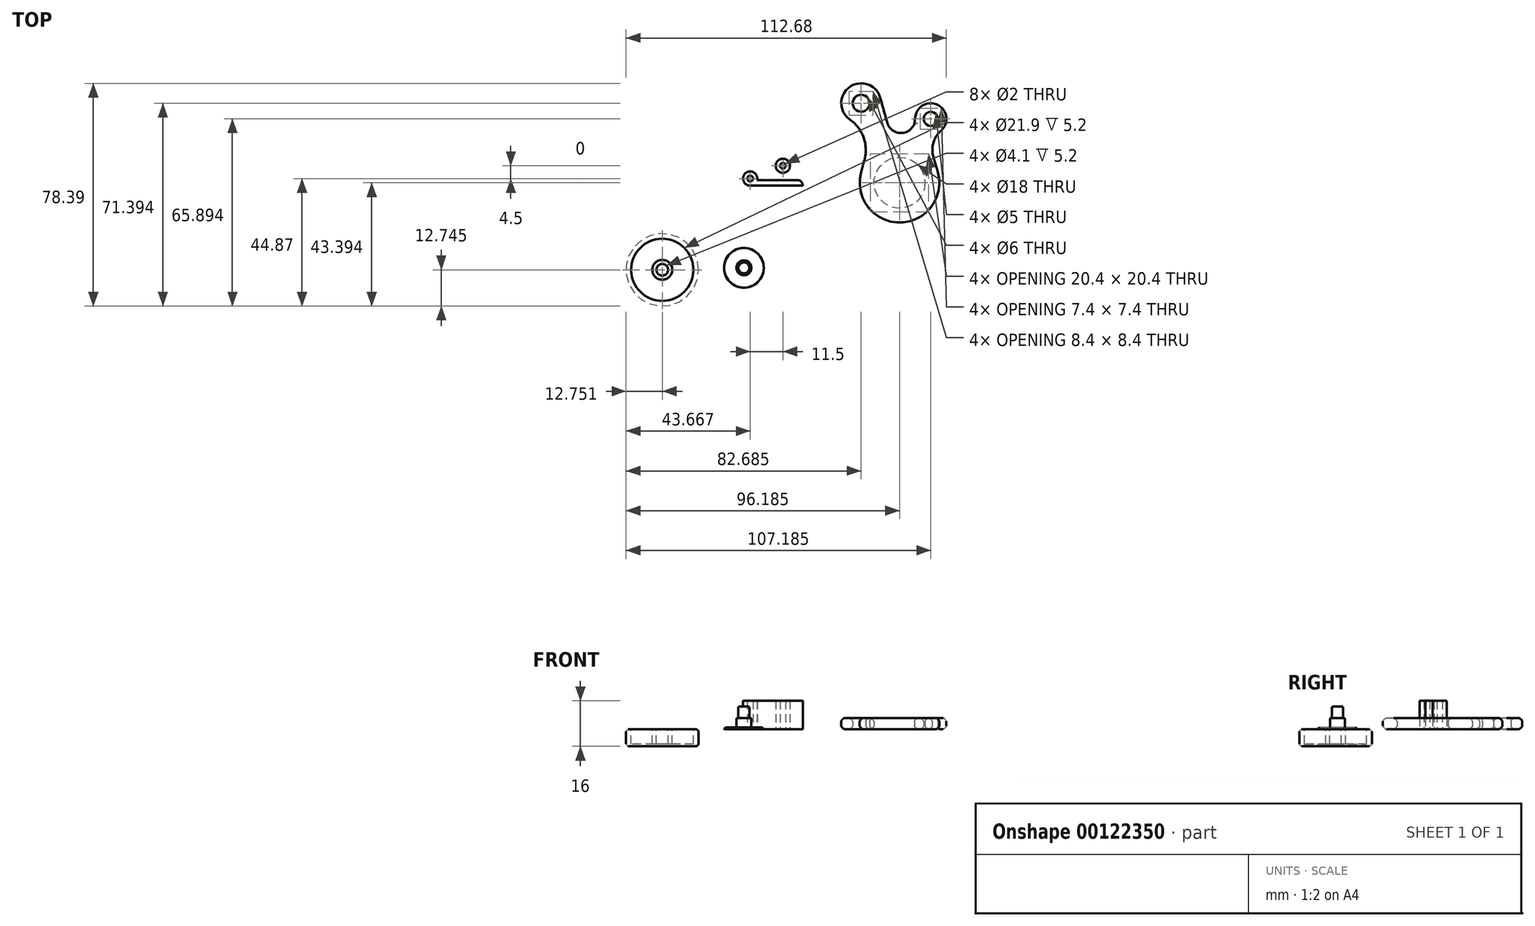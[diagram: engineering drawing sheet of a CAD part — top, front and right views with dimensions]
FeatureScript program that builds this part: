
annotation { "Feature Type Name" : "Feature", "Feature Type Description" : "" }
export const myFeature = defineFeature(function(context is Context, id is Id, definition is map)
    precondition{}
    {
        {
            var Q0;
            Q0=qCreatedBy(makeId("Top.planeOp"),FACE);
            var sketch = newSketch(context, id + "F0", { "sketchPlane" : qUnion([Q0])});
            skCircle(sketch, "E0", {"center": v(-12.84, 2.5) * mm, "radius": 2.5 * mm});
            skCircle(sketch, "E1", {"center": v(-12.84, 2.5) * mm, "radius": 1 * mm});
            skLineSegment(sketch, "E2", {"start": v(-12.84, 0) * mm, "end": v(5.66, 0) * mm});
            skLineSegment(sketch, "E3", {"start": v(-15.34, 2.5) * mm, "end": v(-15.34, 0.8) * mm});
            skArc(sketch, "E4", {"start": v(5.66, 0) * mm, "mid": v(5.07, 1.41) * mm, "end": v(3.66, 2) * mm});
            skLineSegment(sketch, "E5", {"start": v(3.66, 2) * mm, "end": v(-10.4, 2) * mm});
            skCircle(sketch, "E6", {"center": v(-1.34, 7) * mm, "radius": 1 * mm});
            skCircle(sketch, "E7", {"center": v(-1.34, 7) * mm, "radius": 2.5 * mm});
            skArc(sketch, "E8", {"start": v(-1.47, 9.5) * mm, "mid": v(-9.08, 11.1) * mm, "end": v(-13.7, 4.84) * mm});
            skLineSegment(sketch, "E9", {"start": v(-6.52, 11.57) * mm, "end": v(-11.51, 11.57) * mm});
            skArc(sketch, "E10", {"start": v(-11.32, 4.49) * mm, "mid": v(-8.57, 8.7) * mm, "end": v(-3.56, 8.15) * mm});
            skCircle(sketch, "E11", {"center": v(26.17, 29.02) * mm, "radius": 3 * mm});
            skCircle(sketch, "E12", {"center": v(26.17, 29.02) * mm, "radius": 7 * mm});
            skCircle(sketch, "E13", {"center": v(50.67, 23.52) * mm, "radius": 2.5 * mm});
            skCircle(sketch, "E14", {"center": v(50.67, 23.52) * mm, "radius": 5.5 * mm});
            skCircle(sketch, "E15", {"center": v(39.67, 1.02) * mm, "radius": 14 * mm});
            skCircle(sketch, "E16", {"center": v(39.67, 1.02) * mm, "radius": 9 * mm});
            skLineSegment(sketch, "E17", {"start": v(19.17, 29.02) * mm, "end": v(19.17, 34.36) * mm});
            skLineSegment(sketch, "E18", {"start": v(56.17, 23.52) * mm, "end": v(56.17, 35.81) * mm});
            skLineSegment(sketch, "E19", {"start": v(26.17, 36.02) * mm, "end": v(44.62, 36.02) * mm});
            skLineSegment(sketch, "E20", {"start": v(39.67, -12.98) * mm, "end": v(58, -12.98) * mm});
            skLineSegment(sketch, "E21", {"start": v(44.95, 22.03) * mm, "end": v(45.22, 24.2) * mm});
            skLineSegment(sketch, "E22", {"start": v(32.92, 30.91) * mm, "end": v(35.36, 22.18) * mm});
            skArc(sketch, "E23", {"start": v(35.36, 22.18) * mm, "mid": v(40.1, 18.52) * mm, "end": v(44.95, 22.03) * mm});
            skLineSegment(sketch, "E24", {"start": v(26.15, 4.64) * mm, "end": v(27.37, 9.2) * mm});
            skArc(sketch, "E25", {"start": v(27.37, 9.2) * mm, "mid": v(27.01, 17.05) * mm, "end": v(22.2, 23.26) * mm});
            skLineSegment(sketch, "E26", {"start": v(53.08, 5.07) * mm, "end": v(51.6, 9.93) * mm});
            skArc(sketch, "E27", {"start": v(51.6, 9.93) * mm, "mid": v(51.57, 15.06) * mm, "end": v(54.3, 19.4) * mm});
            skCircle(sketch, "E28", {"center": v(-43.76, -29.62) * mm, "radius": 12.75 * mm});
            skCircle(sketch, "E29.0", {"center": v(-43.76, -29.62) * mm, "radius": 10.95 * mm});
            skCircle(sketch, "E30", {"center": v(-43.76, -29.62) * mm, "radius": 3.5 * mm});
            skCircle(sketch, "E31", {"center": v(-43.76, -29.62) * mm, "radius": 2.05 * mm});
            skCircle(sketch, "E32", {"center": v(-15.05, -28.93) * mm, "radius": 7 * mm});
            skCircle(sketch, "E33", {"center": v(-15.05, -28.93) * mm, "radius": 2.6 * mm});
            skCircle(sketch, "E34", {"center": v(-15.05, -28.93) * mm, "radius": 1.95 * mm});
            skSolve(sketch);
        }
        {
            var Q0;
            Q0=makeQuery(id+"F0.imprint","IMPRINT",FACE,{"disambiguationData":[TD([[makeQuery(id+"F0.imprint","IMPRINT",EDGE,{"derivedFrom":sQuery(id+"F0.wireOp",EDGE,"E6")}),-1.0]])]});
            var Q1;
            {var subQ6=sQuery(id+"F0.wireOp",EDGE,"E10");Q1=makeQuery(id+"F0.imprint","IMPRINT",FACE,{"disambiguationData":[TD([[makeQuery(id+"F0.imprint","IMPRINT",EDGE,{"derivedFrom":subQ6}),1.0]])]});}
            var Q2;
            Q2=makeQuery(id+"F0.imprint","IMPRINT",FACE,{"disambiguationData":[TD([[makeQuery(id+"F0.imprint","IMPRINT",EDGE,{"derivedFrom":sQuery(id+"F0.wireOp",EDGE,"E1")}),-1.0]])]});
            var Q3;
            {var subQ0=sQuery(id+"F0.wireOp",EDGE,"E2");Q3=makeQuery(id+"F0.imprint","IMPRINT",FACE,{"disambiguationData":[TD([[makeQuery(id+"F0.imprint","IMPRINT",EDGE,{"derivedFrom":subQ0}),1.0]])]});}
            extrude(context, id + "F1", {"entities" : qUnion([Q0, Q1, Q2, Q3]), "depth" : 10 * mm});
        }
        {
            var Q0;
            {var subQ0=sQuery(id+"F0.wireOp",EDGE,"E21");Q0=makeQuery(id+"F0.imprint","IMPRINT",FACE,{"disambiguationData":[TD([[makeQuery(id+"F0.imprint","IMPRINT",EDGE,{"derivedFrom":subQ0}),-1.0]])]});}
            var Q1;
            Q1=makeQuery(id+"F0.imprint","IMPRINT",FACE,{"disambiguationData":[TD([[makeQuery(id+"F0.imprint","IMPRINT",EDGE,{"derivedFrom":sQuery(id+"F0.wireOp",EDGE,"E11")}),-1.0]])]});
            var Q2;
            Q2=makeQuery(id+"F0.imprint","IMPRINT",FACE,{"disambiguationData":[TD([[makeQuery(id+"F0.imprint","IMPRINT",EDGE,{"derivedFrom":sQuery(id+"F0.wireOp",EDGE,"E13")}),-1.0]])]});
            var Q3;
            Q3=makeQuery(id+"F0.imprint","IMPRINT",FACE,{"disambiguationData":[TD([[makeQuery(id+"F0.imprint","IMPRINT",EDGE,{"derivedFrom":sQuery(id+"F0.wireOp",EDGE,"E16")}),-1.0]])]});
            extrude(context, id + "F2", {"entities" : qUnion([Q0, Q1, Q2, Q3]), "depth" : 4 * mm});
        }
        {
            var Q0;
            Q0=makeQuery(id+"F2.opExtrude","SWEPT_FACE",FACE,{"disambiguationData":[OSD([sQuery(id+"F0.wireOp",EDGE,"E16")])]});
            var Q1;
            Q1=makeQuery(id+"F2.opExtrude","SWEPT_FACE",FACE,{"disambiguationData":[OSD([sQuery(id+"F0.wireOp",EDGE,"E15")])]});
            var Q2;
            Q2=makeQuery(id+"F2.opExtrude","SWEPT_FACE",FACE,{"disambiguationData":[OSD([sQuery(id+"F0.wireOp",EDGE,"E13")])]});
            var Q3;
            Q3=makeQuery(id+"F2.opExtrude","SWEPT_FACE",FACE,{"disambiguationData":[OSD([sQuery(id+"F0.wireOp",EDGE,"E11")])]});
            fillet(context, id + "F3", {"entities" : qUnion([Q0, Q1, Q2, Q3]), "radius" : 1.2 * mm, "tangentPropagation" : true, "rho" : 0.2, "crossSection" : FilletCrossSection.CONIC, "allowEdgeOverflow" : false});
        }
        {
            var Q0;
            Q0=makeQuery(id+"F0.imprint","IMPRINT",FACE,{"disambiguationData":[TD([[makeQuery(id+"F0.imprint","IMPRINT",EDGE,{"derivedFrom":sQuery(id+"F0.wireOp",EDGE,"E28")}),1.0]])]});
            var Q1;
            Q1=makeQuery(id+"F0.imprint","IMPRINT",FACE,{"disambiguationData":[TD([[makeQuery(id+"F0.imprint","IMPRINT",EDGE,{"derivedFrom":sQuery(id+"F0.wireOp",EDGE,"E29.0")}),1.0]])]});
            var Q2;
            Q2=makeQuery(id+"F0.imprint","IMPRINT",FACE,{"disambiguationData":[TD([[makeQuery(id+"F0.imprint","IMPRINT",EDGE,{"derivedFrom":sQuery(id+"F0.wireOp",EDGE,"E30")}),1.0]])]});
            var Q3;
            Q3=makeQuery(id+"F0.imprint","IMPRINT",FACE,{"disambiguationData":[TD([[makeQuery(id+"F0.imprint","IMPRINT",EDGE,{"derivedFrom":sQuery(id+"F0.wireOp",EDGE,"E31")}),1.0]])]});
            extrude(context, id + "F4", {"entities" : qUnion([Q0, Q1, Q2, Q3]), "oppositeDirection" : true, "depth" : 6 * mm});
        }
        {
            var Q0;
            Q0=makeQuery(id+"F0.imprint","IMPRINT",FACE,{"disambiguationData":[TD([[makeQuery(id+"F0.imprint","IMPRINT",EDGE,{"derivedFrom":sQuery(id+"F0.wireOp",EDGE,"E29.0")}),1.0]])]});
            var Q1;
            Q1=makeQuery(id+"F0.imprint","IMPRINT",FACE,{"disambiguationData":[TD([[makeQuery(id+"F0.imprint","IMPRINT",EDGE,{"derivedFrom":sQuery(id+"F0.wireOp",EDGE,"E31")}),1.0]])]});
            extrude(context, id + "F5", {"entities" : qUnion([Q0, Q1]), "operationType" : NewBodyOperationType.REMOVE, "oppositeDirection" : true, "depth" : 5.2 * mm});
        }
        {
            var Q0;
            Q0=makeQuery(id+"F4.opExtrude","CAP_EDGE",EDGE,{"disambiguationData":[OSD([sQuery(id+"F0.wireOp",EDGE,"E28")])],"isStart":false});
            var Q1;
            Q1=makeQuery(id+"F4.opExtrude","CAP_EDGE",EDGE,{"disambiguationData":[OSD([sQuery(id+"F0.wireOp",EDGE,"E28")])],"isStart":true});
            fillet(context, id + "F6", {"entities" : qUnion([Q0, Q1]), "radius" : 0.8 * mm, "tangentPropagation" : true, "rho" : 0.2, "crossSection" : FilletCrossSection.CONIC, "allowEdgeOverflow" : false});
        }
        {
            var Q0;
            Q0=makeQuery(id+"F0.imprint","IMPRINT",FACE,{"disambiguationData":[TD([[makeQuery(id+"F0.imprint","IMPRINT",EDGE,{"derivedFrom":sQuery(id+"F0.wireOp",EDGE,"E32")}),1.0]])]});
            var Q1;
            Q1=makeQuery(id+"F0.imprint","IMPRINT",FACE,{"disambiguationData":[TD([[makeQuery(id+"F0.imprint","IMPRINT",EDGE,{"derivedFrom":sQuery(id+"F0.wireOp",EDGE,"E33")}),1.0]])]});
            var Q2;
            Q2=makeQuery(id+"F0.imprint","IMPRINT",FACE,{"disambiguationData":[TD([[makeQuery(id+"F0.imprint","IMPRINT",EDGE,{"derivedFrom":sQuery(id+"F0.wireOp",EDGE,"E34")}),1.0]])]});
            extrude(context, id + "F7", {"entities" : qUnion([Q0, Q1, Q2]), "depth" : 0.6 * mm});
        }
        {
            var Q0;
            Q0=makeQuery(id+"F0.imprint","IMPRINT",FACE,{"disambiguationData":[TD([[makeQuery(id+"F0.imprint","IMPRINT",EDGE,{"derivedFrom":sQuery(id+"F0.wireOp",EDGE,"E33")}),1.0]])]});
            var Q1;
            Q1=makeQuery(id+"F0.imprint","IMPRINT",FACE,{"disambiguationData":[TD([[makeQuery(id+"F0.imprint","IMPRINT",EDGE,{"derivedFrom":sQuery(id+"F0.wireOp",EDGE,"E34")}),1.0]])]});
            extrude(context, id + "F8", {"entities" : qUnion([Q0, Q1]), "operationType" : NewBodyOperationType.ADD, "depth" : 4 * mm});
        }
        {
            var Q0;
            Q0=makeQuery(id+"F0.imprint","IMPRINT",FACE,{"disambiguationData":[TD([[makeQuery(id+"F0.imprint","IMPRINT",EDGE,{"derivedFrom":sQuery(id+"F0.wireOp",EDGE,"E34")}),1.0]])]});
            extrude(context, id + "F9", {"entities" : qUnion([Q0]), "operationType" : NewBodyOperationType.ADD, "depth" : 8 * mm});
        }
        {
            var Q0;
            Q0=makeQuery(id+"F7.opExtrude","CAP_EDGE",EDGE,{"disambiguationData":[OSD([sQuery(id+"F0.wireOp",EDGE,"E32")])],"isStart":false});
            fillet(context, id + "F10", {"entities" : qUnion([Q0]), "radius" : 0.6 * mm, "tangentPropagation" : true, "rho" : 0.1, "crossSection" : FilletCrossSection.CONIC, "allowEdgeOverflow" : false});
        }
        {
            var Q0;
            Q0=makeQuery(id+"F8.opExtrude","CAP_EDGE",EDGE,{"disambiguationData":[OSD([sQuery(id+"F0.wireOp",EDGE,"E33")])],"isStart":false});
            var Q1;
            Q1=makeQuery(id+"F9.opExtrude","CAP_EDGE",EDGE,{"disambiguationData":[OSD([sQuery(id+"F0.wireOp",EDGE,"E34")])],"isStart":false});
            fillet(context, id + "F11", {"entities" : qUnion([Q0, Q1]), "radius" : 0.3 * mm, "tangentPropagation" : true, "rho" : 0.1, "crossSection" : FilletCrossSection.CONIC, "allowEdgeOverflow" : false});
        }
    });
